# Revit family: Toilet_Tissue_Dispenser-Bradley_Corp-522
name_source: partatom
category: Specialty Equipment
revit_build: Autodesk Revit MEP 2012 (Build: 20110309_2315(x64)
units: mm (PartAtom-declared; Revit-internal decimal feet)

## types (1)
- 522
    ADA Compliant = No
    Assembly Code = C1030200
    Buy American Act = To Be Determined
    Default Elevation = 48 "
    Depth = 4.25 "
    Description = Toilet Tissue Dispenser
    Height = 2.438 "
    Low Emitting Material = No
    Manufacturer = Bradley Corporation
    MasterFormat Number = 10 28 00
    MasterFormat Title = Toilet, Bath, and Laundry Accessories
    Model = 522
    OmniClass Table 21 Number = 21-03 10 90 40
    OmniClass Table 21 Title = Toilet, Bath, and Laundry Accessories
    OmniClass Table 23 Number = 23.31.25.21
    OmniClass Table 23 Title = Toilet Paper Dispensers
    Percentage of Recycled Content = 0
    Product Tech Data URL - English = http://bradleycorp.com
    Specifications URL = http://www.bradleycorp.com
    Type Comments = Diecast Zinc, Chrome Plated Finish
    URL = http://www.bradleycorp.com
    Unit Material = Metal - Bradley Corp - Chrome
    Version = 2.0
    Warranty Information = Complete Unit 1 Year Warranty. This Warranty does not cover installation or any other labor charges and does not apply to any units which have been damaged by abuse, improper installation, imporper maintanence, or altered in any way.
    Width = 10.5 "

## geometry (parser evidence)
native form markers: Blend x8, Sweep x1
no freeform markers — native parametric forms only
